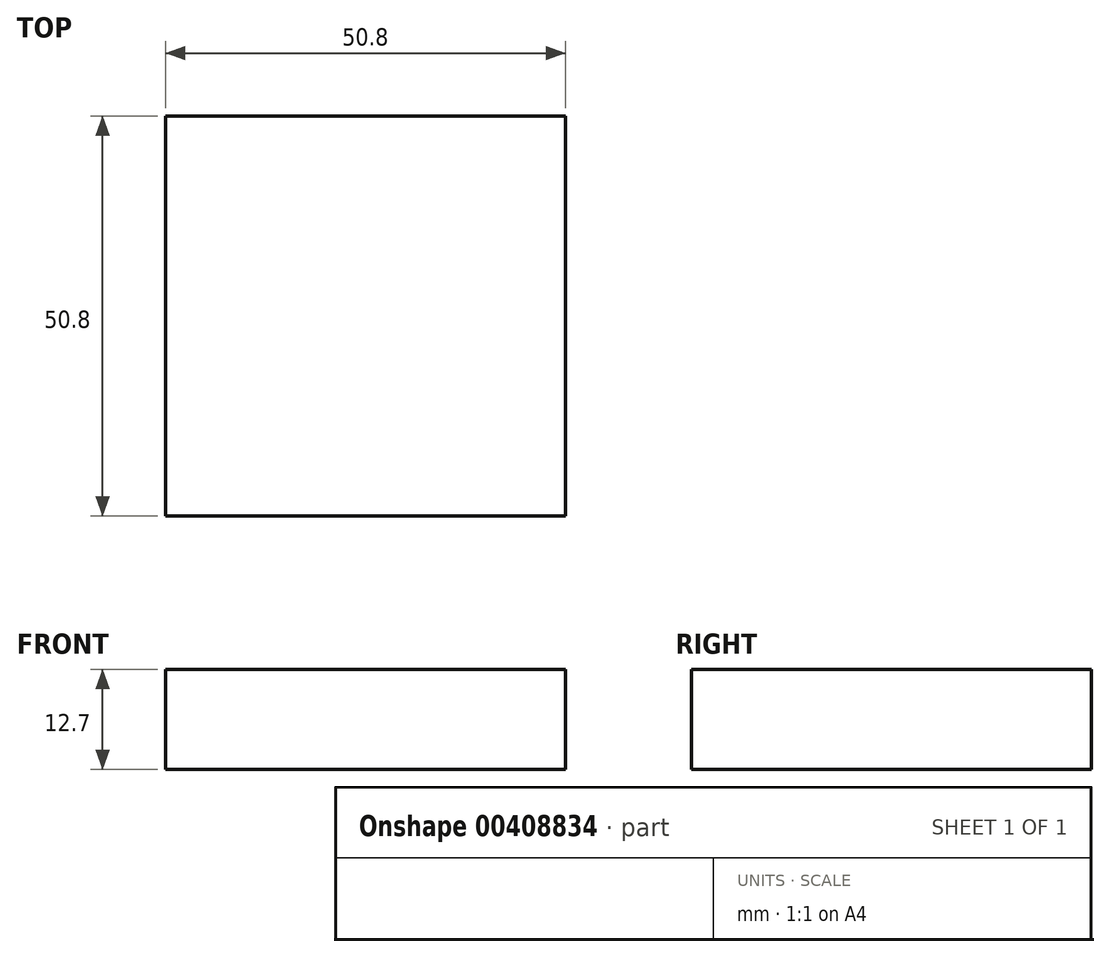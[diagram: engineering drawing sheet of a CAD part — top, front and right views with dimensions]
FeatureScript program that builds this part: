
annotation { "Feature Type Name" : "Feature", "Feature Type Description" : "" }
export const myFeature = defineFeature(function(context is Context, id is Id, definition is map)
    precondition{}
    {
        {
            var Q0;
            Q0=qCreatedBy(makeId("Top.planeOp"),FACE);
            var sketch = newSketch(context, id + "F0", { "sketchPlane" : qUnion([Q0])});
            skLineSegment(sketch, "E0.bottom", {"start": v(-25.4, -25.4) * mm, "end": v(25.4, -25.4) * mm});
            skLineSegment(sketch, "E0.top", {"start": v(-25.4, 25.4) * mm, "end": v(25.4, 25.4) * mm});
            skLineSegment(sketch, "E0.left", {"start": v(-25.4, -25.4) * mm, "end": v(-25.4, 25.4) * mm});
            skLineSegment(sketch, "E0.right", {"start": v(25.4, -25.4) * mm, "end": v(25.4, 25.4) * mm});
            skPoint(sketch, "E0.middle", {"position": v(0, 0) * mm});
            skSolve(sketch);
        }
        {
            var Q0;
            Q0 = qSketchRegion(id + "F0", true);
            extrude(context, id + "F1", {"entities" : qUnion([Q0]), "depth" : 12.7 * mm});
        }
    });
